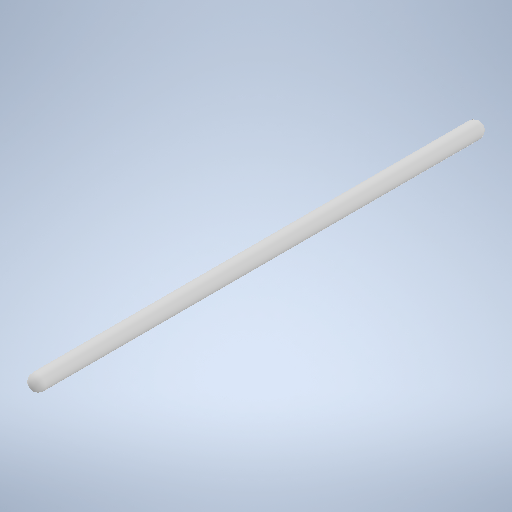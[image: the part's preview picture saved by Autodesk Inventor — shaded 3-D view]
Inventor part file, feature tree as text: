
AUTODESK INVENTOR PART (.ipt)
format: ipt  version: 2025 (Build 290162010, 162A)  size: 252,416 bytes
history: native  units: in
note: dims shown in document units (in); Inventor stores cm internally (conversion verified against a paired STEP export)
features: revolve x1, sketch x1
ambient origin geometry x8: Origin, YZ Plane, XZ Plane, XY Plane, X Axis, Y Axis, Z Axis, Center Point
bodies: Solid1 (feature_tree)
feature tree (2):
  revolve  "Revolution1"  [1 undecoded]
  sketch  "Sketch1"  dims[d0=2.2835in d1=0.0787in d2=90.0deg]
note: 1 required parameter value undecoded (feature->parameter linkage not recoverable at this tier; creation-order binding heuristic only, values carry confidence <= 0.55)
